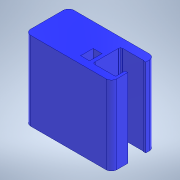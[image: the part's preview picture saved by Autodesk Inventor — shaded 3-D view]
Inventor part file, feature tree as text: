
AUTODESK INVENTOR PART (.ipt)
format: ipt  version: 2022 (Build 260153000, 153)  size: 167,936 bytes
history: native  units: mm
features: other x7, reference x3, direct_edit x1, extrude x1, sketch x1, move_body x1
ambient origin geometry x8: Origin, YZ Plane, XZ Plane, XY Plane, X Axis, Y Axis, Z Axis, Center Point
bodies: Solid1 (feature_tree)
feature tree (14):
  other  "Z Belt Housing.ipt"
  direct_edit  "Direct Edit1"
  extrude  "Extrusion1"  Depth=10.0mm TaperAngle=0.0deg
  other  "Solid1::Z Belt Housing.ipt"
  other  "TaggingFeature1"
  sketch  "Sketch1"  dims[d0=10.0mm d1=0.0mm d2=0.0mm d3=10.0mm d4=2.0mm d5=5.0mm d6=0.0mm d7=0.0mm]
  reference  "Reference1"
  reference  "Reference2"
  reference  "Reference3"
  move_body  "Move1"
  parser-record x1  (decoder bookkeeping rows leaked as tree rows — omitted from the tree; the rows remain in map.json)
  other  "Bibble0.iam"
  other  "Alternate Z Drive Assembly:1"
  other  "GT2 Pulley 16T:1"
note: 1 file-system path scrubbed to <path> (originals preserved in map.json)
